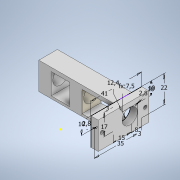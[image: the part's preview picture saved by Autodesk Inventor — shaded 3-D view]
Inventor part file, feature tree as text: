
AUTODESK INVENTOR PART (.ipt)
format: ipt  version: 2020.3 (Build 243373000, 373)  size: 320,000 bytes
history: native  units: mm
features: sketch x4, extrude x4, plane x1
ambient origin geometry x8: Origin, YZ Plane, XZ Plane, XY Plane, X Axis, Y Axis, Z Axis, Center Point
bodies: Body1 (feature_tree)
feature tree (9):
  sketch  "Sketch1"  dims[d10=41.0mm d11=22.0mm]
  extrude  "Extrusion5"  Depth=22.0mm
  extrude  "Extrusion6"  Depth=10.0mm
  extrude  "Extrusion7"  Depth=8.0mm
  plane  "Work Plane1"
  sketch  "Sketch5"  dims[d17=8.0mm d18=2.8mm]
  extrude  "Extrusion8"  Depth=10.0mm
  sketch  "Sketch4"  dims[d12=15.0mm d15=10.0mm]
  sketch  "Sketch6"  dims[d19=2.8mm d20=12.4mm d22=10.0mm d23=10.0mm d24=35.0mm d25=3.0mm d26=7.5mm d27=17.0mm d28=3.0mm d29=6.0mm d30=0.0mm d31=50.0mm d32=0.0mm d33=10.0mm d34=0.0mm d35=25.0mm d36=10.0mm d37=0.0mm d38=12.4mm d39=12.4mm]
